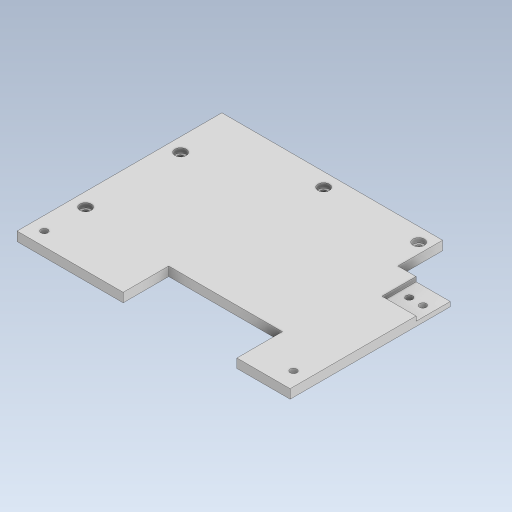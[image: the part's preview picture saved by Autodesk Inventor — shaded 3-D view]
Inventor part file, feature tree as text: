
AUTODESK INVENTOR PART (.ipt)
format: ipt  version: 2023.5 (Build 275446000, 446)  size: 155,648 bytes
history: native  units: in
note: dims shown in document units (in); Inventor stores cm internally (conversion verified against a paired STEP export)
features: extrude x2, sketch x1
ambient origin geometry x8: Origin, YZ Plane, XZ Plane, XY Plane, X Axis, Y Axis, Z Axis, Center Point
bodies: Solid1 (feature_tree)
feature tree (3):
  sketch  "Sketch1"  dims[d28=0.1575in d29=0.0in d30=0.0787in d31=0.0in d32=0.2953in d33=0.4724in d34=0.4724in d35=0.2953in d36=0.0in d37=0.0in d38=0.315in]
  extrude  "Extrusion1"  Depth=0.0787in TaperAngle=0.0deg
  extrude  "Extrusion2"  Depth=0.315in
